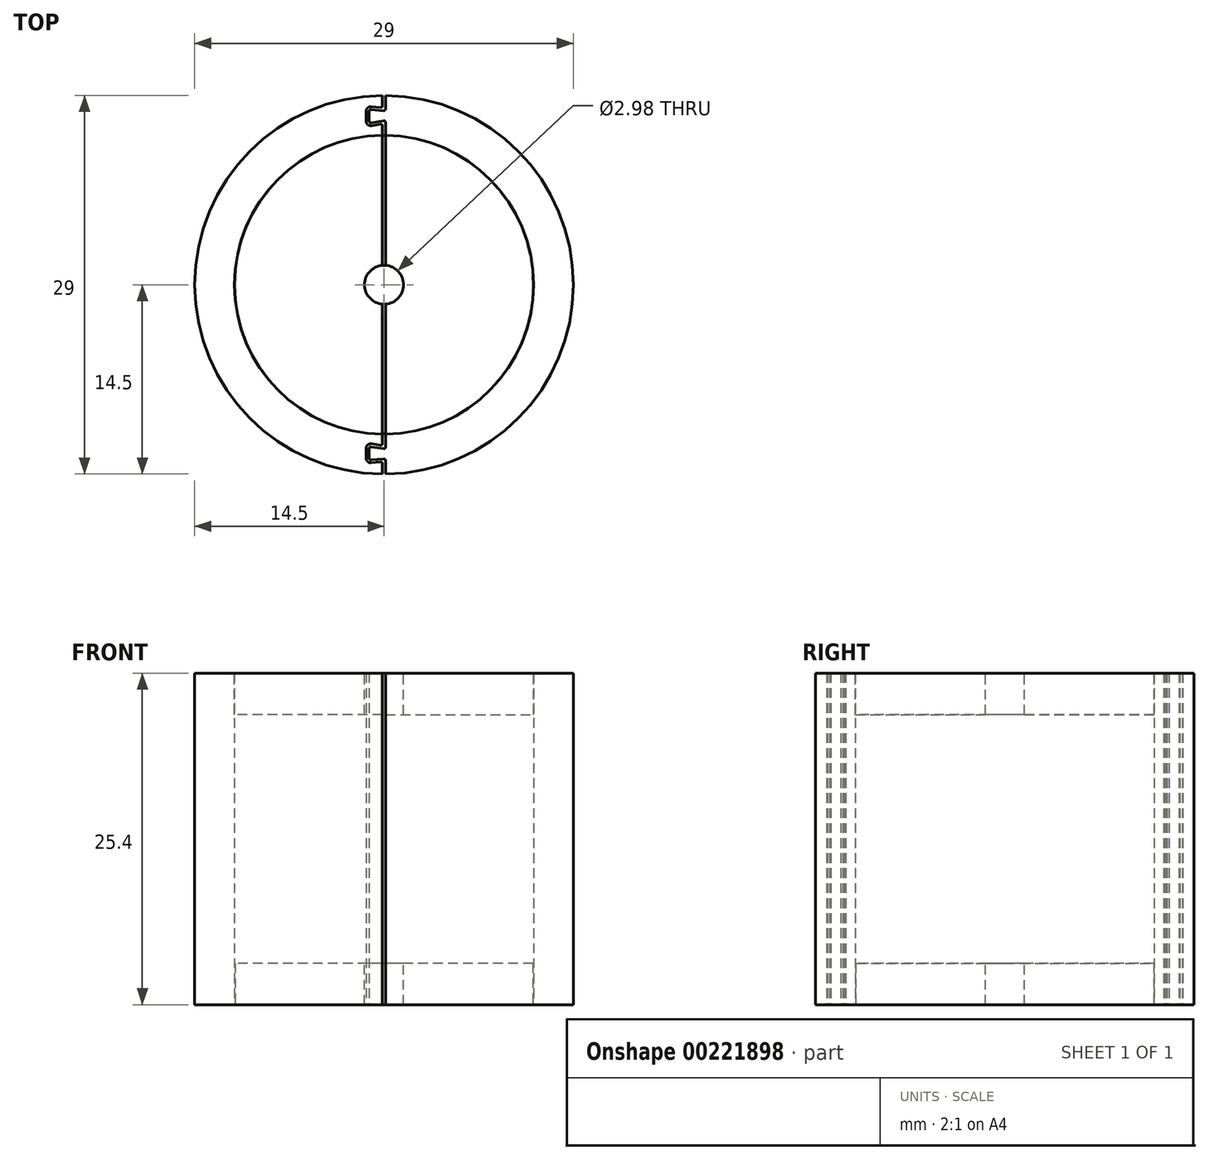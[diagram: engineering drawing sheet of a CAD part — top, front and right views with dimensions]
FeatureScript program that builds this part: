
annotation { "Feature Type Name" : "Feature", "Feature Type Description" : "" }
export const myFeature = defineFeature(function(context is Context, id is Id, definition is map)
    precondition{}
    {
        {
            var Q0;
            Q0=qCreatedBy(makeId("Top.planeOp"),FACE);
            var sketch = newSketch(context, id + "F0", { "sketchPlane" : qUnion([Q0])});
            skArc(sketch, "E0", {"start": v(-0.12, 14.5) * mm, "mid": v(-14.5, 0) * mm, "end": v(-0.12, -14.5) * mm});
            skArc(sketch, "E1", {"start": v(0.12, -1.52) * mm, "mid": v(1.52, 0) * mm, "end": v(0.12, 1.52) * mm});
            skArc(sketch, "E2.0", {"start": v(-0.12, 11.45) * mm, "mid": v(-11.45, 0) * mm, "end": v(-0.12, -11.45) * mm});
            skLineSegment(sketch, "E3", {"start": v(-0.02, 13.34) * mm, "end": v(-1, 13.41) * mm});
            skLineSegment(sketch, "E4", {"start": v(-1.14, 13.28) * mm, "end": v(-1.14, 12.54) * mm});
            skLineSegment(sketch, "E5", {"start": v(-1, 12.41) * mm, "end": v(-0.03, 12.56) * mm});
            skPoint(sketch, "E6", {"position": v(0, 12.94) * mm});
            skLineSegment(sketch, "E7", {"start": v(0, 12.94) * mm, "end": v(-1.14, 12.9) * mm, "construction": true});
            skPoint(sketch, "E8.visualSharp", {"position": v(-1.14, 13.42) * mm});
            skArc(sketch, "E8.filletArc", {"start": v(-1, 13.41) * mm, "mid": v(-1.1, 13.38) * mm, "end": v(-1.14, 13.28) * mm});
            skPoint(sketch, "E9.visualSharp", {"position": v(-1.14, 12.39) * mm});
            skArc(sketch, "E9.filletArc", {"start": v(-1.14, 12.54) * mm, "mid": v(-1.1, 12.44) * mm, "end": v(-1, 12.41) * mm});
            skLineSegment(sketch, "E10.0", {"start": v(-0.96, 12.19) * mm, "end": v(-0.27, 12.3) * mm});
            skLineSegment(sketch, "E10.1", {"start": v(-0.26, 13.58) * mm, "end": v(-0.98, 13.64) * mm});
            skArc(sketch, "E10.2", {"start": v(-0.98, 13.64) * mm, "mid": v(-1.26, 13.54) * mm, "end": v(-1.37, 13.28) * mm});
            skLineSegment(sketch, "E10.3", {"start": v(-1.37, 13.28) * mm, "end": v(-1.37, 12.54) * mm});
            skArc(sketch, "E10.4", {"start": v(-1.37, 12.54) * mm, "mid": v(-1.25, 12.27) * mm, "end": v(-0.96, 12.19) * mm});
            skLineSegment(sketch, "E11", {"start": v(0.12, 14.5) * mm, "end": v(0.12, 13.47) * mm});
            skLineSegment(sketch, "E12.MirrorCS", {"start": v(-0.12, 14.5) * mm, "end": v(-0.12, 13.71) * mm});
            skLineSegment(sketch, "E13.trimOffspring", {"start": v(-0.12, 12.17) * mm, "end": v(-0.12, 11.45) * mm});
            skLineSegment(sketch, "E14.trimOffspring", {"start": v(0.12, 12.43) * mm, "end": v(0.12, 11.45) * mm});
            skPoint(sketch, "E15.visualSharp", {"position": v(-0.12, 12.32) * mm});
            skArc(sketch, "E15.filletArc", {"start": v(-0.12, 12.17) * mm, "mid": v(-0.16, 12.27) * mm, "end": v(-0.27, 12.3) * mm});
            skPoint(sketch, "E16.visualSharp", {"position": v(0.12, 12.59) * mm});
            skArc(sketch, "E16.filletArc", {"start": v(0.12, 12.43) * mm, "mid": v(0.07, 12.53) * mm, "end": v(-0.03, 12.56) * mm});
            skPoint(sketch, "E17.visualSharp", {"position": v(-0.12, 13.57) * mm});
            skArc(sketch, "E17.filletArc", {"start": v(-0.26, 13.58) * mm, "mid": v(-0.16, 13.62) * mm, "end": v(-0.12, 13.71) * mm});
            skPoint(sketch, "E18.visualSharp", {"position": v(0.12, 13.32) * mm});
            skArc(sketch, "E18.filletArc", {"start": v(-0.02, 13.34) * mm, "mid": v(0.07, 13.37) * mm, "end": v(0.12, 13.47) * mm});
            skArc(sketch, "E19.MirrorCS", {"start": v(-0.26, -13.58) * mm, "mid": v(-0.16, -13.62) * mm, "end": v(-0.12, -13.71) * mm});
            skArc(sketch, "E20.MirrorCS", {"start": v(-1, -13.41) * mm, "mid": v(-1.1, -13.38) * mm, "end": v(-1.14, -13.28) * mm});
            skPoint(sketch, "E21.MirrorP", {"position": v(-0.12, -13.57) * mm});
            skArc(sketch, "E22.MirrorCS", {"start": v(-0.02, -13.34) * mm, "mid": v(0.07, -13.37) * mm, "end": v(0.12, -13.47) * mm});
            skArc(sketch, "E23.MirrorCS", {"start": v(0.12, -12.43) * mm, "mid": v(0.07, -12.53) * mm, "end": v(-0.03, -12.56) * mm});
            skLineSegment(sketch, "E24.MirrorCS", {"start": v(-1.37, -13.28) * mm, "end": v(-1.37, -12.54) * mm});
            skArc(sketch, "E25.MirrorCS", {"start": v(-1.37, -12.54) * mm, "mid": v(-1.25, -12.27) * mm, "end": v(-0.96, -12.19) * mm});
            skArc(sketch, "E26.MirrorCS", {"start": v(-0.12, -12.17) * mm, "mid": v(-0.16, -12.27) * mm, "end": v(-0.27, -12.3) * mm});
            skLineSegment(sketch, "E27.MirrorCS", {"start": v(-1, -12.41) * mm, "end": v(-0.03, -12.56) * mm});
            skLineSegment(sketch, "E28.MirrorCS", {"start": v(0.12, -14.5) * mm, "end": v(0.12, -13.47) * mm});
            skPoint(sketch, "E29.MirrorP", {"position": v(-1.14, -12.39) * mm});
            skLineSegment(sketch, "E30.MirrorCS", {"start": v(-0.12, -14.5) * mm, "end": v(-0.12, -13.71) * mm});
            skLineSegment(sketch, "E31.MirrorCS", {"start": v(-0.96, -12.19) * mm, "end": v(-0.27, -12.3) * mm});
            skPoint(sketch, "E32.MirrorP", {"position": v(-0.12, -12.32) * mm});
            skPoint(sketch, "E33.MirrorP", {"position": v(0.12, -12.59) * mm});
            skLineSegment(sketch, "E34.MirrorCS", {"start": v(-0.02, -13.34) * mm, "end": v(-1, -13.41) * mm});
            skLineSegment(sketch, "E35.MirrorCS", {"start": v(-1.14, -13.28) * mm, "end": v(-1.14, -12.54) * mm});
            skPoint(sketch, "E36.MirrorP", {"position": v(0.12, -13.32) * mm});
            skArc(sketch, "E37.MirrorCS", {"start": v(-0.98, -13.64) * mm, "mid": v(-1.26, -13.54) * mm, "end": v(-1.37, -13.28) * mm});
            skPoint(sketch, "E38.MirrorP", {"position": v(-1.14, -13.42) * mm});
            skLineSegment(sketch, "E39.MirrorCS", {"start": v(-0.26, -13.58) * mm, "end": v(-0.98, -13.64) * mm});
            skArc(sketch, "E40.MirrorCS", {"start": v(-1.14, -12.54) * mm, "mid": v(-1.1, -12.44) * mm, "end": v(-1, -12.41) * mm});
            skPoint(sketch, "E41.MirrorP", {"position": v(0, -12.94) * mm});
            skLineSegment(sketch, "E42.MirrorCS", {"start": v(-0.12, -12.17) * mm, "end": v(-0.12, -11.45) * mm});
            skLineSegment(sketch, "E43.MirrorCS", {"start": v(0.12, -12.43) * mm, "end": v(0.12, -11.45) * mm});
            skArc(sketch, "E44.trimOffspring", {"start": v(0.12, -14.5) * mm, "mid": v(14.5, 0) * mm, "end": v(0.12, 14.5) * mm});
            skArc(sketch, "E45.trimOffspring", {"start": v(0.12, -11.45) * mm, "mid": v(11.45, 0) * mm, "end": v(0.12, 11.45) * mm});
            skLineSegment(sketch, "E46", {"start": v(-0.12, 11.45) * mm, "end": v(-0.12, 1.52) * mm});
            skLineSegment(sketch, "E47", {"start": v(0.12, 11.45) * mm, "end": v(0.12, 1.52) * mm});
            skLineSegment(sketch, "E48.MirrorCS", {"start": v(-0.12, -11.45) * mm, "end": v(-0.12, -1.52) * mm});
            skLineSegment(sketch, "E49.MirrorCS", {"start": v(0.12, -11.45) * mm, "end": v(0.12, -1.52) * mm});
            skArc(sketch, "E50.trimOffspring", {"start": v(-0.12, 1.52) * mm, "mid": v(-1.52, 0) * mm, "end": v(-0.12, -1.52) * mm});
            skSolve(sketch);
        }
        {
            var Q0;
            Q0=makeQuery(id+"F0.imprint","IMPRINT",FACE,{"disambiguationData":[TD([[makeQuery(id+"F0.imprint","IMPRINT",EDGE,{"derivedFrom":sQuery(id+"F0.wireOp",EDGE,"E0")}),1.0]])]});
            extrude(context, id + "F1", {"entities" : qUnion([Q0]), "depth" : 25.4 * mm});
        }
        {
            var Q0;
            Q0=makeQuery(id+"F0.imprint","IMPRINT",FACE,{"disambiguationData":[TD([[makeQuery(id+"F0.imprint","IMPRINT",EDGE,{"derivedFrom":sQuery(id+"F0.wireOp",EDGE,"E3")}),1.0]])]});
            extrude(context, id + "F2", {"entities" : qUnion([Q0]), "depth" : 25.4 * mm});
        }
        {
            var Q0;
            Q0=qCreatedBy(makeId("Top.planeOp"),FACE);
            var sketch = newSketch(context, id + "F3", { "sketchPlane" : qUnion([Q0])});
            skCircle(sketch, "E51", {"center": v(0, 0) * mm, "radius": 11.4 * mm});
            skSolve(sketch);
        }
        {
            var Q0;
            Q0=makeQuery(id+"F3.imprint","IMPRINT",FACE,{"disambiguationData":[TD([[makeQuery(id+"F3.imprint","IMPRINT",EDGE,{"derivedFrom":sQuery(id+"F3.wireOp",EDGE,"E51")}),1.0]])]});
            extrude(context, id + "F4", {"entities" : qUnion([Q0]), "depth" : 3.17 * mm});
        }
        {
            var Q0;
            Q0=makeQuery(id+"F2.opExtrude","CAP_FACE",FACE,{"disambiguationData":[OSD([sQuery(id+"F0.wireOp",EDGE,"E3"),sQuery(id+"F0.wireOp",EDGE,"E4"),sQuery(id+"F0.wireOp",EDGE,"E5"),sQuery(id+"F0.wireOp",EDGE,"E8.filletArc"),sQuery(id+"F0.wireOp",EDGE,"E9.filletArc"),sQuery(id+"F0.wireOp",EDGE,"E11"),sQuery(id+"F0.wireOp",EDGE,"E14.trimOffspring"),sQuery(id+"F0.wireOp",EDGE,"E16.filletArc"),sQuery(id+"F0.wireOp",EDGE,"E18.filletArc"),sQuery(id+"F0.wireOp",EDGE,"E20.MirrorCS"),sQuery(id+"F0.wireOp",EDGE,"E22.MirrorCS"),sQuery(id+"F0.wireOp",EDGE,"E23.MirrorCS"),sQuery(id+"F0.wireOp",EDGE,"E27.MirrorCS"),sQuery(id+"F0.wireOp",EDGE,"E34.MirrorCS"),sQuery(id+"F0.wireOp",EDGE,"E35.MirrorCS"),sQuery(id+"F0.wireOp",EDGE,"E40.MirrorCS"),sQuery(id+"F0.wireOp",EDGE,"E28.MirrorCS"),sQuery(id+"F0.wireOp",EDGE,"E43.MirrorCS"),sQuery(id+"F0.wireOp",EDGE,"E44.trimOffspring"),sQuery(id+"F0.wireOp",EDGE,"E45.trimOffspring")])],"isStart":false});
            cPlane(context, id + "F5", {"entities" : qUnion([Q0]), "cplaneType" : CPlaneType.OFFSET, "offset" : 0 * mm, "width" : 152.4 * mm, "height" : 152.4 * mm});
        }
        {
            var Q0;
            Q0=qCreatedBy(id+"F5.planeOp",FACE);
            var sketch = newSketch(context, id + "F6", { "sketchPlane" : qUnion([Q0])});
            skArc(sketch, "E52", {"start": v(0.12, -11.45) * mm, "mid": v(11.45, 0) * mm, "end": v(0.12, 11.45) * mm});
            skLineSegment(sketch, "E53", {"start": v(-0.12, -11.45) * mm, "end": v(-0.12, -11.2) * mm, "construction": true});
            skLineSegment(sketch, "E54", {"start": v(-0.12, -11.45) * mm, "end": v(-0.12, -11.45) * mm});
            skLineSegment(sketch, "E55", {"start": v(-0.12, -11.45) * mm, "end": v(-0.12, 11.45) * mm});
            skLineSegment(sketch, "E56", {"start": v(0.12, -11.45) * mm, "end": v(0.12, 11.45) * mm});
            skArc(sketch, "E57.trimOffspring", {"start": v(-0.12, 11.45) * mm, "mid": v(-11.45, 0) * mm, "end": v(-0.12, -11.45) * mm});
            skSolve(sketch);
        }
        {
            var Q0;
            Q0=makeQuery(id+"F6.imprint","IMPRINT",FACE,{"disambiguationData":[TD([[makeQuery(id+"F6.imprint","IMPRINT",EDGE,{"derivedFrom":sQuery(id+"F6.wireOp",EDGE,"E55")}),1.0]])]});
            var Q1;
            Q1=makeQuery(id+"F6.imprint","IMPRINT",FACE,{"disambiguationData":[TD([[makeQuery(id+"F6.imprint","IMPRINT",EDGE,{"derivedFrom":sQuery(id+"F6.wireOp",EDGE,"E52")}),1.0]])]});
            extrude(context, id + "F7", {"entities" : qUnion([Q0, Q1]), "oppositeDirection" : true, "depth" : 3.17 * mm});
        }
        {
            var Q0;
            Q0=qCreatedBy(makeId("Top.planeOp"),FACE);
            var sketch = newSketch(context, id + "F8", { "sketchPlane" : qUnion([Q0])});
            skCircle(sketch, "E58", {"center": v(0, 0) * mm, "radius": 1.5 * mm});
            skSolve(sketch);
        }
        {
            var Q0;
            Q0=makeQuery(id+"F3.imprint","IMPRINT",FACE,{"disambiguationData":[TD([[makeQuery(id+"F3.imprint","IMPRINT",EDGE,{"derivedFrom":sQuery(id+"F3.wireOp",EDGE,"E51")}),1.0]])]});
            extrude(context, id + "F9", {"entities" : qUnion([Q0]), "operationType" : NewBodyOperationType.ADD, "depth" : 3.17 * mm});
        }
        {
            var Q0;
            Q0 = qSketchRegion(id + "F8", true);
            extrude(context, id + "F10", {"entities" : qUnion([Q0]), "operationType" : NewBodyOperationType.REMOVE, "oppositeDirection" : true, "depth" : 10.4 * mm, "hasSecondDirection" : true, "secondDirectionOppositeDirection" : false, "secondDirectionDepth" : 34.54 * mm});
        }
    });
